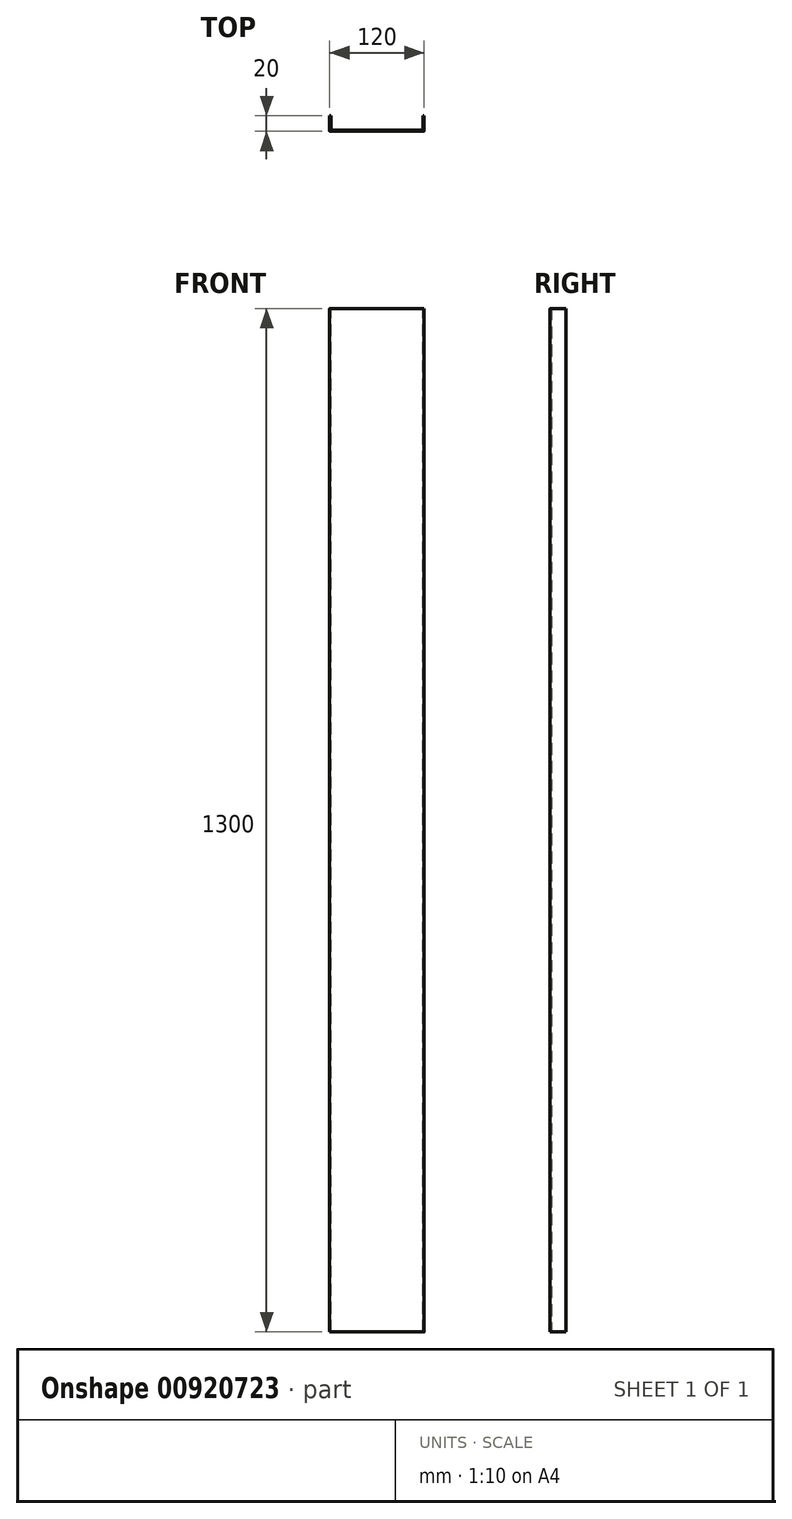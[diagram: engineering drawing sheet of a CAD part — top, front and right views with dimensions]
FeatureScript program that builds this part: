
annotation { "Feature Type Name" : "Feature", "Feature Type Description" : "" }
export const myFeature = defineFeature(function(context is Context, id is Id, definition is map)
    precondition{}
    {
        {
            var Q0;
            Q0=qCreatedBy(makeId("Top.planeOp"),FACE);
            var sketch = newSketch(context, id + "F0", { "sketchPlane" : qUnion([Q0])});
            skLineSegment(sketch, "E0.bottom", {"start": v(59.6, 20) * mm, "end": v(-59.6, 20) * mm});
            skLineSegment(sketch, "E0.top", {"start": v(59.6, -20) * mm, "end": v(-59.6, -20) * mm});
            skLineSegment(sketch, "E0.left", {"start": v(60, 19.6) * mm, "end": v(60, -19.6) * mm});
            skLineSegment(sketch, "E0.right", {"start": v(-60, 19.6) * mm, "end": v(-60, -19.6) * mm});
            skPoint(sketch, "E0.middle", {"position": v(0, 0) * mm});
            skPoint(sketch, "E1.visualSharp", {"position": v(-60, 20) * mm});
            skArc(sketch, "E1.filletArc", {"start": v(-59.6, 20) * mm, "mid": v(-59.88, 19.88) * mm, "end": v(-60, 19.6) * mm});
            skPoint(sketch, "E2.visualSharp", {"position": v(-60, -20) * mm});
            skArc(sketch, "E2.filletArc", {"start": v(-60, -19.6) * mm, "mid": v(-59.88, -19.88) * mm, "end": v(-59.6, -20) * mm});
            skPoint(sketch, "E3.visualSharp", {"position": v(60, -20) * mm});
            skArc(sketch, "E3.filletArc", {"start": v(59.6, -20) * mm, "mid": v(59.88, -19.88) * mm, "end": v(60, -19.6) * mm});
            skPoint(sketch, "E4.visualSharp", {"position": v(60, 20) * mm});
            skArc(sketch, "E4.filletArc", {"start": v(60, 19.6) * mm, "mid": v(59.88, 19.88) * mm, "end": v(59.6, 20) * mm});
            skLineSegment(sketch, "E5.0", {"start": v(58.5, 18.5) * mm, "end": v(58.5, -18.5) * mm});
            skLineSegment(sketch, "E5.1", {"start": v(58.5, 18.5) * mm, "end": v(-58.5, 18.5) * mm});
            skLineSegment(sketch, "E5.2", {"start": v(-58.5, 18.5) * mm, "end": v(-58.5, -18.5) * mm});
            skLineSegment(sketch, "E5.3", {"start": v(58.5, -18.5) * mm, "end": v(-58.5, -18.5) * mm});
            skSolve(sketch);
        }
        {
            var Q0;
            Q0=qSketchRegion(id+"F0",true);
            extrude(context, id + "F1", {"entities" : qUnion([Q0]), "depth" : 1300 * mm, "offsetDistance" : 25 * mm});
        }
        {
            var Q0;
            Q0=makeQuery(id+"F1.opExtrude","CAP_FACE",FACE,{"disambiguationData":[OSD([sQuery(id+"F0.wireOp",EDGE,"E0.bottom"),sQuery(id+"F0.wireOp",EDGE,"E0.top"),sQuery(id+"F0.wireOp",EDGE,"E0.left"),sQuery(id+"F0.wireOp",EDGE,"E0.right"),sQuery(id+"F0.wireOp",EDGE,"E1.filletArc"),sQuery(id+"F0.wireOp",EDGE,"E2.filletArc"),sQuery(id+"F0.wireOp",EDGE,"E3.filletArc"),sQuery(id+"F0.wireOp",EDGE,"E4.filletArc"),sQuery(id+"F0.wireOp",EDGE,"E5.0"),sQuery(id+"F0.wireOp",EDGE,"E5.1"),sQuery(id+"F0.wireOp",EDGE,"E5.2"),sQuery(id+"F0.wireOp",EDGE,"E5.3")])],"isStart":false});
            var sketch = newSketch(context, id + "F2", { "sketchPlane" : qUnion([Q0])});
            skLineSegment(sketch, "E6", {"start": v(-58.5, 0) * mm, "end": v(-60, 0) * mm});
            skLineSegment(sketch, "E7", {"start": v(58.5, 0) * mm, "end": v(60, 0) * mm});
            skSolve(sketch);
        }
        {
            var Q0;
            {var subQ3=sQuery(id+"F2.wireOp",EDGE,"E6");Q0=makeQuery(id+"F2.imprint","IMPRINT",FACE,{"disambiguationData":[TD([[makeQuery(id+"F2.imprint","IMPRINT",EDGE,{"derivedFrom":subQ3}),-1.0]])]});}
            extrude(context, id + "F3", {"entities" : qUnion([Q0]), "operationType" : NewBodyOperationType.REMOVE, "oppositeDirection" : true, "depth" : 1300 * mm, "offsetDistance" : 25 * mm});
        }
    });
